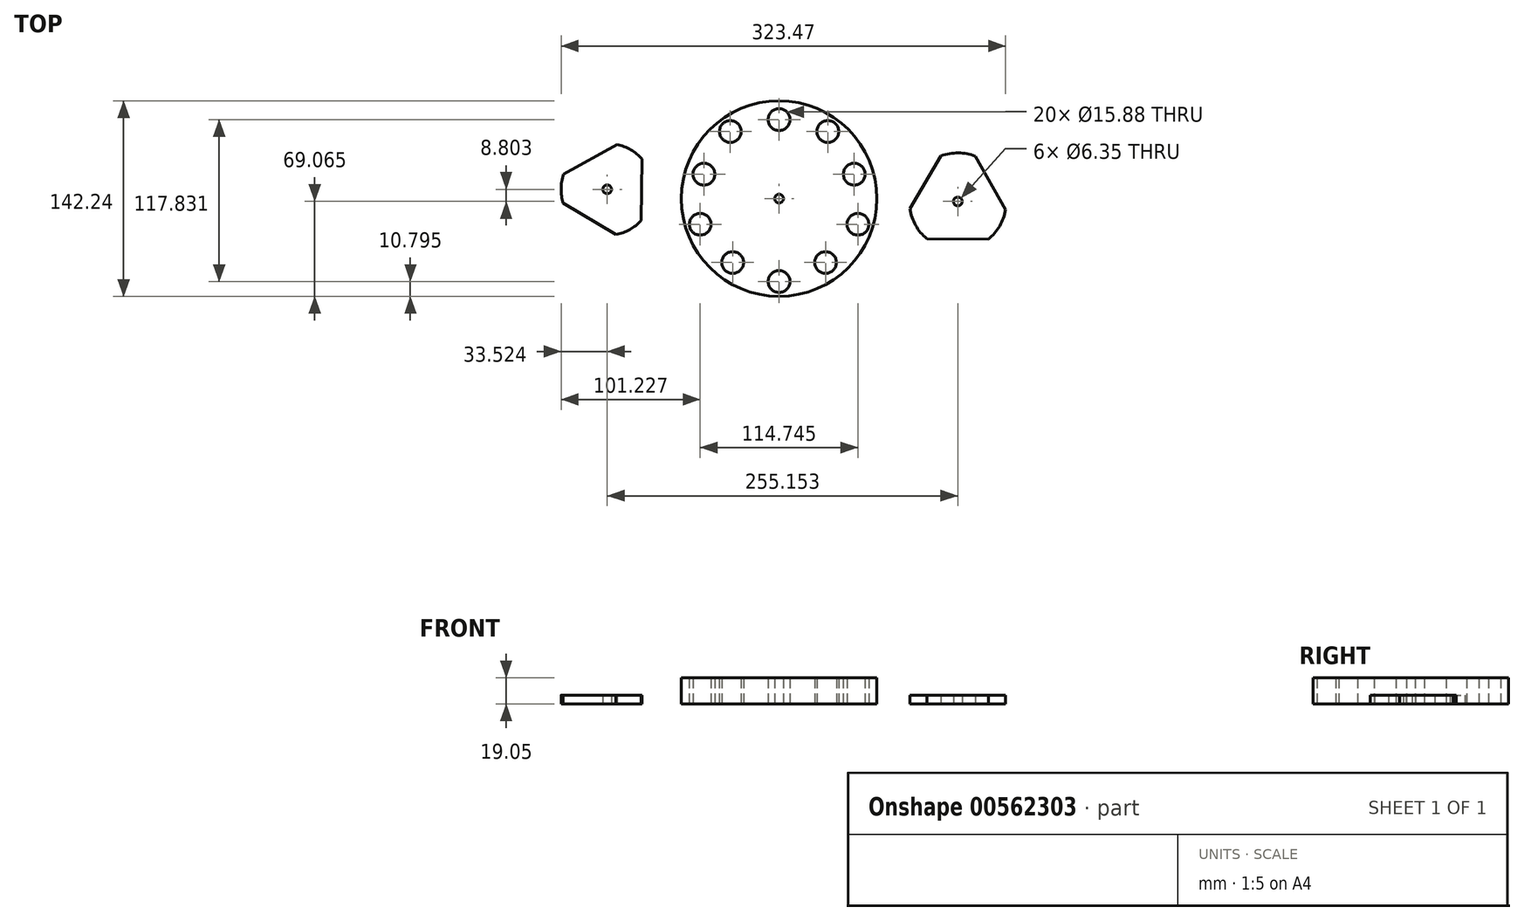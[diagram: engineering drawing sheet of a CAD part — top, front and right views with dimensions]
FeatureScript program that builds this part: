
annotation { "Feature Type Name" : "Feature", "Feature Type Description" : "" }
export const myFeature = defineFeature(function(context is Context, id is Id, definition is map)
    precondition{}
    {
        {
            var Q0;
            Q0=qCreatedBy(makeId("Top.planeOp"),FACE);
            var sketch = newSketch(context, id + "F0", { "sketchPlane" : qUnion([Q0])});
            skCircle(sketch, "E0", {"center": v(0, 0) * mm, "radius": 3.18 * mm});
            skCircle(sketch, "E1", {"center": v(0, 0) * mm, "radius": 57.5 * mm, "construction": true});
            skCircle(sketch, "E2", {"center": v(0, 0) * mm, "radius": 60.33 * mm, "construction": true});
            skCircle(sketch, "E3", {"center": v(0, 57.5) * mm, "radius": 7.94 * mm});
            skCircle(sketch, "E4", {"center": v(0, -60.33) * mm, "radius": 7.94 * mm});
            skCircle(sketch, "E5.1.0", {"center": v(-54.7, 17.77) * mm, "radius": 7.94 * mm});
            skCircle(sketch, "E5.1.1", {"center": v(57.37, -18.64) * mm, "radius": 7.94 * mm});
            skCircle(sketch, "E5.2.0", {"center": v(-33.8, -46.52) * mm, "radius": 7.94 * mm});
            skCircle(sketch, "E5.2.1", {"center": v(35.46, 48.8) * mm, "radius": 7.94 * mm});
            skCircle(sketch, "E5.3.0", {"center": v(33.8, -46.52) * mm, "radius": 7.94 * mm});
            skCircle(sketch, "E5.3.1", {"center": v(-35.46, 48.8) * mm, "radius": 7.94 * mm});
            skCircle(sketch, "E5.4.0", {"center": v(54.7, 17.77) * mm, "radius": 7.94 * mm});
            skCircle(sketch, "E5.4.1", {"center": v(-57.37, -18.64) * mm, "radius": 7.94 * mm});
            skCircle(sketch, "E6", {"center": v(0, 0) * mm, "radius": 71.12 * mm});
            skSolve(sketch);
        }
        {
            var Q0;
            Q0=qCreatedBy(makeId("Top.planeOp"),FACE);
            var sketch = newSketch(context, id + "F1", { "sketchPlane" : qUnion([Q0])});
            skArc(sketch, "E7", {"start": v(-156.8, 17.6) * mm, "mid": v(-158.6, 7.2) * mm, "end": v(-157.08, -3.25) * mm});
            skCircle(sketch, "E8.cCircle", {"center": v(-125.08, 6.75) * mm, "radius": 24.96 * mm, "construction": true});
            skLineSegment(sketch, "E8.0", {"start": v(-118.62, -26.15) * mm, "end": v(-157.08, -3.25) * mm});
            skLineSegment(sketch, "E8.1", {"start": v(-156.8, 17.6) * mm, "end": v(-117.73, 39.46) * mm});
            skLineSegment(sketch, "E8.2", {"start": v(-99.81, 28.8) * mm, "end": v(-100.42, -15.97) * mm});
            skPoint(sketch, "E8.0.midPoint", {"position": v(-137.85, -14.7) * mm});
            skPoint(sketch, "E9.orphan", {"position": v(-99.53, 49.64) * mm});
            skPoint(sketch, "E10.orphan", {"position": v(-175, 7.42) * mm});
            skPoint(sketch, "E11.orphan", {"position": v(-100.7, -36.82) * mm});
            skCircle(sketch, "E12", {"center": v(-125.08, 6.75) * mm, "radius": 3.18 * mm});
            skArc(sketch, "E13", {"start": v(95.2, -7.5) * mm, "mid": v(99.36, -19.45) * mm, "end": v(107.47, -29.18) * mm});
            skCircle(sketch, "E14.cCircle", {"center": v(130.08, -2.05) * mm, "radius": 27.3 * mm, "construction": true});
            skLineSegment(sketch, "E14.0", {"start": v(95.2, -7.5) * mm, "end": v(117.9, 31.08) * mm});
            skLineSegment(sketch, "E14.1", {"start": v(142.81, 30.87) * mm, "end": v(164.87, -8.07) * mm});
            skLineSegment(sketch, "E14.2", {"start": v(152.23, -29.55) * mm, "end": v(107.47, -29.18) * mm});
            skPoint(sketch, "E14.0.midPoint", {"position": v(106.54, 11.8) * mm});
            skPoint(sketch, "E15.orphan", {"position": v(82.55, -28.97) * mm});
            skPoint(sketch, "E16.orphan", {"position": v(130.53, 52.56) * mm});
            skPoint(sketch, "E17.orphan", {"position": v(177.15, -29.76) * mm});
            skCircle(sketch, "E18", {"center": v(130.08, -2.05) * mm, "radius": 3.18 * mm});
            skArc(sketch, "E19.trimOffspring", {"start": v(-99.81, 28.8) * mm, "mid": v(-107.92, 35.55) * mm, "end": v(-117.73, 39.46) * mm});
            skArc(sketch, "E20.trimOffspring", {"start": v(-118.62, -26.15) * mm, "mid": v(-108.7, -22.51) * mm, "end": v(-100.42, -15.97) * mm});
            skArc(sketch, "E21.trimOffspring", {"start": v(142.81, 30.87) * mm, "mid": v(130.37, 33.25) * mm, "end": v(117.9, 31.08) * mm});
            skArc(sketch, "E22.trimOffspring", {"start": v(152.23, -29.55) * mm, "mid": v(160.5, -19.96) * mm, "end": v(164.87, -8.07) * mm});
            skSolve(sketch);
        }
        {
            var Q0;
            Q0=makeQuery(id+"F0.imprint","IMPRINT",FACE,{"disambiguationData":[TD([[makeQuery(id+"F0.imprint","IMPRINT",EDGE,{"derivedFrom":sQuery(id+"F0.wireOp",EDGE,"E0")}),-1.0]])]});
            extrude(context, id + "F2", {"entities" : qUnion([Q0]), "depth" : 19.05 * mm, "offsetDistance" : 25.4 * mm});
        }
        {
            var Q0;
            Q0 = qSketchRegion(id + "F1", true);
            extrude(context, id + "F3", {"entities" : qUnion([Q0]), "depth" : 6.35 * mm, "offsetDistance" : 25.4 * mm});
        }
    });
